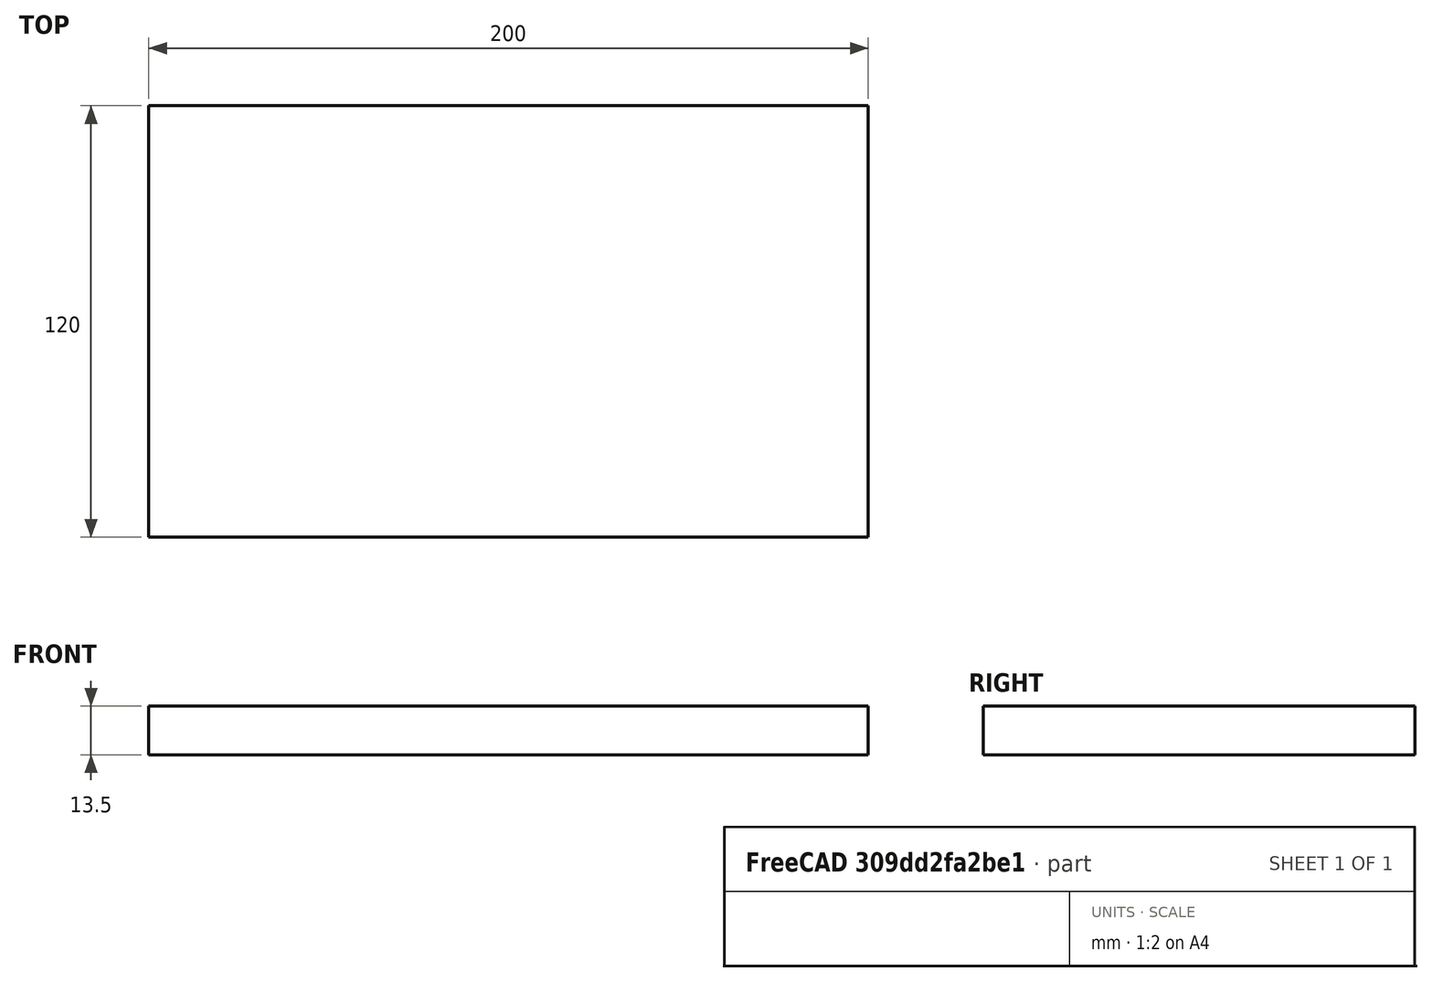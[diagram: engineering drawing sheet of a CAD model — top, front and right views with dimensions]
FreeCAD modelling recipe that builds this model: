
FCSTD DOCUMENT  (FreeCAD 0.19R24276 (Git))
Label: Osnovanie_120x200x13_5
License: All rights reserved
LicenseURL: http://en.wikipedia.org/wiki/All_rights_reserved
objects: Sketcher::SketchObject×1, PartDesign::Pad×1, PartDesign::Body×1
note: 4 computed .brp shape members not serialized (recipe doc carries the construction recipe); baked Part::Feature solids carry a one-line shape summary decoded from their .brp

FEATURE [Sketcher::SketchObject] Sketch
  FullyConstrained = true
  MapMode = 5
  Support = -> [XY_Plane]
  sketch-geometry (4):
    g0: LineSegment StartX=0 StartY=0 StartZ=0 EndX=200 EndY=0 EndZ=0
    g1: LineSegment StartX=200 StartY=0 StartZ=0 EndX=200 EndY=120 EndZ=0
    g2: LineSegment StartX=200 StartY=120 StartZ=0 EndX=0 EndY=120 EndZ=0
    g3: LineSegment StartX=0 StartY=120 StartZ=0 EndX=0 EndY=0 EndZ=0
  constraints (11):
    c: Coincident(g0,g1)
    c: Coincident(g1,g2)
    c: Coincident(g2,g3)
    c: Coincident(g3,g0)
    c: Horizontal(g0)
    c: Horizontal(g2)
    c: Vertical(g1)
    c: Vertical(g3)
    c: Coincident(g0,g-1)
    c: DistanceX(g0,g0) = 200
    c: DistanceY(g3,g3) = 120
FEATURE [PartDesign::Pad] Pad
  Direction = (1,1,1)
  Length = 13.5
  Length2 = 100
  Profile = -> Sketch
  Type = 0
FEATURE [PartDesign::Body] Body
  Group = -> [Sketch,Pad]
  Origin = -> Origin
  Tip = -> Pad
